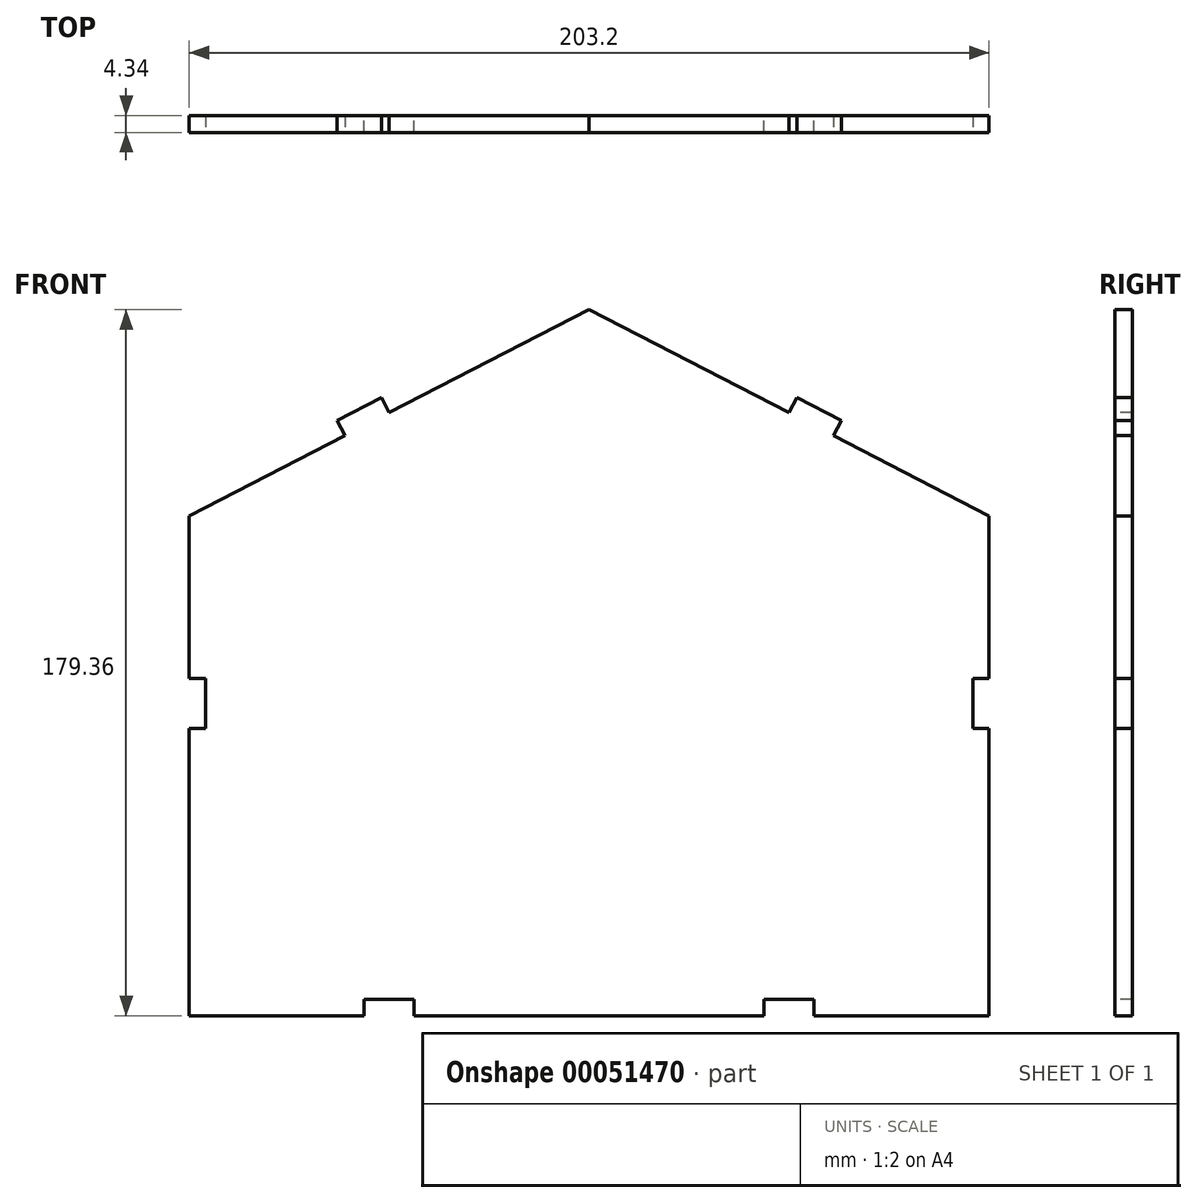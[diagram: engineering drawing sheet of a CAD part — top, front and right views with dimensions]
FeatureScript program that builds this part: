
annotation { "Feature Type Name" : "Feature", "Feature Type Description" : "" }
export const myFeature = defineFeature(function(context is Context, id is Id, definition is map)
    precondition{}
    {
        {
            var Q0;
            Q0=qCreatedBy(makeId("Front.planeOp"),FACE);
            var sketch = newSketch(context, id + "F0", { "sketchPlane" : qUnion([Q0])});
            skLineSegment(sketch, "E0", {"start": v(0, 100.27) * mm, "end": v(-101.6, 47.9) * mm});
            skLineSegment(sketch, "E1", {"start": v(0, 100.27) * mm, "end": v(101.6, 47.9) * mm});
            skLineSegment(sketch, "E2", {"start": v(-101.6, 47.9) * mm, "end": v(-101.6, -79.1) * mm});
            skLineSegment(sketch, "E3", {"start": v(-101.6, -79.1) * mm, "end": v(-57.15, -79.1) * mm});
            skLineSegment(sketch, "E4", {"start": v(101.6, -79.1) * mm, "end": v(101.6, 47.9) * mm});
            skLineSegment(sketch, "E5.0", {"start": v(-50.8, 100.27) * mm, "end": v(-50.8, 74.09) * mm, "construction": true});
            skLineSegment(sketch, "E6.0", {"start": v(50.8, 100.27) * mm, "end": v(50.8, 74.09) * mm, "construction": true});
            skLineSegment(sketch, "E7", {"start": v(-50.8, 74.09) * mm, "end": v(-52.79, 77.95) * mm});
            skLineSegment(sketch, "E8", {"start": v(-52.79, 77.95) * mm, "end": v(-64.08, 72.13) * mm});
            skLineSegment(sketch, "E9", {"start": v(-64.08, 72.13) * mm, "end": v(-62.09, 68.27) * mm});
            skLineSegment(sketch, "E10", {"start": v(50.8, 74.09) * mm, "end": v(52.79, 77.95) * mm});
            skLineSegment(sketch, "E11", {"start": v(52.79, 77.95) * mm, "end": v(64.08, 72.13) * mm});
            skLineSegment(sketch, "E12", {"start": v(64.08, 72.13) * mm, "end": v(62.09, 68.27) * mm});
            skPoint(sketch, "E13.MirrorCS.start.orphan", {"position": v(-50.8, -74.75) * mm});
            skPoint(sketch, "E14.start.orphan", {"position": v(-44.45, -74.75) * mm});
            skPoint(sketch, "E15.end.orphan", {"position": v(-57.15, -74.75) * mm});
            skLineSegment(sketch, "E16", {"start": v(-44.45, -79.1) * mm, "end": v(-57.15, -79.1) * mm});
            skPoint(sketch, "E17.MirrorCS.start.orphan", {"position": v(50.8, -74.75) * mm});
            skPoint(sketch, "E18.start.orphan", {"position": v(57.15, -74.75) * mm});
            skPoint(sketch, "E19.end.orphan", {"position": v(44.45, -79.1) * mm});
            skPoint(sketch, "E19.start.orphan", {"position": v(44.45, -74.75) * mm});
            skLineSegment(sketch, "E20", {"start": v(50.8, -79.1) * mm, "end": v(44.45, -79.1) * mm});
            skLineSegment(sketch, "E21.trimOffspring", {"start": v(-50.8, -74.75) * mm, "end": v(-50.8, -79.1) * mm, "construction": true});
            skLineSegment(sketch, "E22.trimOffspring", {"start": v(50.8, -74.75) * mm, "end": v(50.8, -79.1) * mm, "construction": true});
            skPoint(sketch, "E23.end.orphan", {"position": v(0, -79.1) * mm});
            skLineSegment(sketch, "E24", {"start": v(0, 100.27) * mm, "end": v(0, -79.1) * mm, "construction": true});
            skLineSegment(sketch, "E25.0", {"start": v(-50.8, 100.27) * mm, "end": v(-50.8, -79.1) * mm, "construction": true});
            skLineSegment(sketch, "E26.0", {"start": v(50.8, 100.27) * mm, "end": v(50.8, -79.1) * mm, "construction": true});
            skLineSegment(sketch, "E27.trimOffspring", {"start": v(-44.45, -79.1) * mm, "end": v(44.45, -79.1) * mm});
            skLineSegment(sketch, "E28.trimOffspring", {"start": v(50.8, -79.1) * mm, "end": v(101.6, -79.1) * mm});
            skLineSegment(sketch, "E29.bottom", {"start": v(-57.15, -79.1) * mm, "end": v(-44.45, -79.1) * mm});
            skLineSegment(sketch, "E29.top", {"start": v(-57.15, -74.75) * mm, "end": v(-44.45, -74.75) * mm});
            skLineSegment(sketch, "E29.left", {"start": v(-57.15, -79.1) * mm, "end": v(-57.15, -74.75) * mm});
            skLineSegment(sketch, "E29.right", {"start": v(-44.45, -79.1) * mm, "end": v(-44.45, -74.75) * mm});
            skLineSegment(sketch, "E30.bottom", {"start": v(44.45, -79.1) * mm, "end": v(57.15, -79.1) * mm});
            skLineSegment(sketch, "E30.top", {"start": v(44.45, -74.75) * mm, "end": v(57.15, -74.75) * mm});
            skLineSegment(sketch, "E30.left", {"start": v(44.45, -79.1) * mm, "end": v(44.45, -74.75) * mm});
            skLineSegment(sketch, "E30.right", {"start": v(57.15, -79.1) * mm, "end": v(57.15, -74.75) * mm});
            skSolve(sketch);
        }
        {
            var Q0;
            Q0=qSketchRegion(id+"F0",true);
            extrude(context, id + "F1", {"entities" : qUnion([Q0]), "oppositeDirection" : true, "depth" : 4.34 * mm});
        }
        {
            var Q0;
            Q0=qCreatedBy(makeId("Front.planeOp"),FACE);
            var sketch = newSketch(context, id + "F2", { "sketchPlane" : qUnion([Q0])});
            skLineSegment(sketch, "E31.bottom", {"start": v(-101.83, 6.57) * mm, "end": v(-97.49, 6.57) * mm});
            skLineSegment(sketch, "E31.top", {"start": v(-101.83, -6.13) * mm, "end": v(-97.49, -6.13) * mm});
            skLineSegment(sketch, "E31.left", {"start": v(-101.83, 6.57) * mm, "end": v(-101.83, -6.13) * mm});
            skLineSegment(sketch, "E31.right", {"start": v(-97.49, 6.57) * mm, "end": v(-97.49, -6.13) * mm});
            skLineSegment(sketch, "E32.MirrorCS", {"start": v(101.83, 6.57) * mm, "end": v(101.83, -6.13) * mm});
            skLineSegment(sketch, "E33.MirrorCS", {"start": v(101.83, 6.57) * mm, "end": v(97.49, 6.57) * mm});
            skLineSegment(sketch, "E34.MirrorCS", {"start": v(97.49, 6.57) * mm, "end": v(97.49, -6.13) * mm});
            skLineSegment(sketch, "E35.MirrorCS", {"start": v(101.83, -6.13) * mm, "end": v(97.49, -6.13) * mm});
            skSolve(sketch);
        }
        {
            var Q0;
            Q0=qSketchRegion(id+"F2",true);
            extrude(context, id + "F3", {"entities" : qUnion([Q0]), "operationType" : NewBodyOperationType.REMOVE, "endBound" : BoundingType.THROUGH_ALL, "oppositeDirection" : true, "depth" : 25.4 * mm});
        }
        {
            var Q0;
            Q0=qCreatedBy(makeId("Front.planeOp"),FACE);
            var sketch = newSketch(context, id + "F4", { "sketchPlane" : qUnion([Q0])});
            skLineSegment(sketch, "E36", {"start": v(0, 100.24) * mm, "end": v(0, -79.76) * mm, "construction": true});
            skLineSegment(sketch, "E37.0", {"start": v(-50.8, 100.24) * mm, "end": v(-50.8, -79.32) * mm, "construction": true});
            skLineSegment(sketch, "E38.0", {"start": v(50.8, 100.24) * mm, "end": v(50.8, -79.76) * mm, "construction": true});
            skLineSegment(sketch, "E39", {"start": v(-50.8, -79.32) * mm, "end": v(-57.15, -79.32) * mm});
            skLineSegment(sketch, "E40", {"start": v(-57.15, -79.32) * mm, "end": v(-57.15, -74.97) * mm});
            skLineSegment(sketch, "E41", {"start": v(-57.15, -74.97) * mm, "end": v(-50.8, -74.97) * mm});
            skLineSegment(sketch, "E42.MirrorCS", {"start": v(-44.45, -74.97) * mm, "end": v(-50.8, -74.97) * mm});
            skLineSegment(sketch, "E43.MirrorCS", {"start": v(-44.45, -79.32) * mm, "end": v(-44.45, -74.97) * mm});
            skLineSegment(sketch, "E44.MirrorCS", {"start": v(-50.8, -79.32) * mm, "end": v(-44.45, -79.32) * mm});
            skLineSegment(sketch, "E45.MirrorCS", {"start": v(57.15, -74.97) * mm, "end": v(50.8, -74.97) * mm});
            skLineSegment(sketch, "E46.MirrorCS", {"start": v(44.45, -74.97) * mm, "end": v(50.8, -74.97) * mm});
            skLineSegment(sketch, "E47.MirrorCS", {"start": v(44.45, -79.32) * mm, "end": v(44.45, -74.97) * mm});
            skLineSegment(sketch, "E48.MirrorCS", {"start": v(50.8, -79.32) * mm, "end": v(44.45, -79.32) * mm});
            skLineSegment(sketch, "E49.MirrorCS", {"start": v(50.8, -79.32) * mm, "end": v(57.15, -79.32) * mm});
            skLineSegment(sketch, "E50.MirrorCS", {"start": v(57.15, -79.32) * mm, "end": v(57.15, -74.97) * mm});
            skSolve(sketch);
        }
        {
            var Q0;
            Q0=qSketchRegion(id+"F4",true);
            extrude(context, id + "F5", {"entities" : qUnion([Q0]), "operationType" : NewBodyOperationType.REMOVE, "endBound" : BoundingType.THROUGH_ALL, "oppositeDirection" : true, "depth" : 25.4 * mm});
        }
    });
